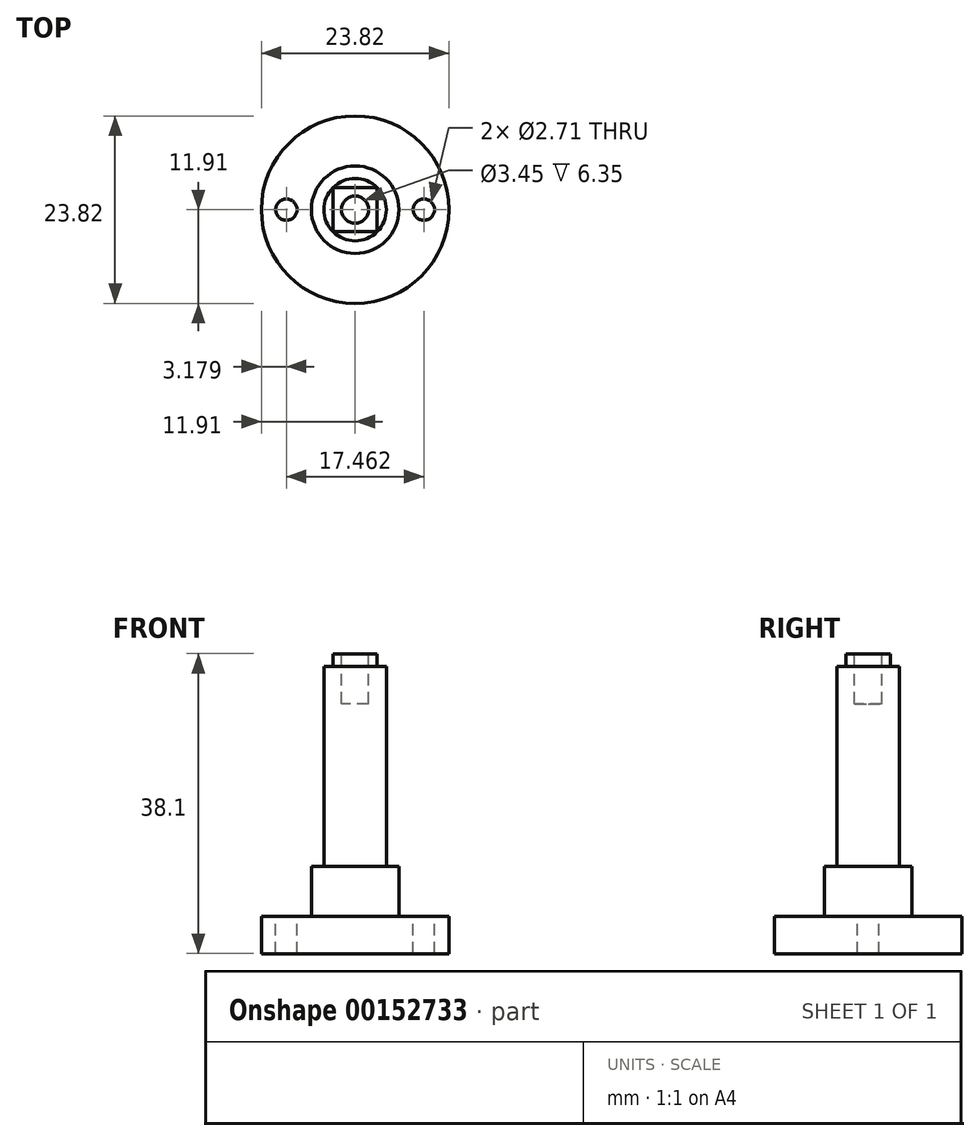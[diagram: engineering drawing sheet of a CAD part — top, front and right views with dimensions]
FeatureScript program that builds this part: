
annotation { "Feature Type Name" : "Feature", "Feature Type Description" : "" }
export const myFeature = defineFeature(function(context is Context, id is Id, definition is map)
    precondition{}
    {
        {
            var Q0;
            Q0=qCreatedBy(makeId("Top.planeOp"),FACE);
            var sketch = newSketch(context, id + "F0", { "sketchPlane" : qUnion([Q0])});
            skCircle(sketch, "E0", {"center": v(0, 0) * mm, "radius": 3.97 * mm});
            skSolve(sketch);
        }
        {
            var Q0;
            Q0 = qSketchRegion(id + "F0", true);
            extrude(context, id + "F1", {"entities" : qUnion([Q0]), "depth" : 25.4 * mm});
        }
        {
            var Q0;
            Q0=makeQuery(id+"F1.opExtrude","CAP_FACE",FACE,{"disambiguationData":[OSD([sQuery(id+"F0.wireOp",EDGE,"E0")])],"isStart":false});
            var sketch = newSketch(context, id + "F2", { "sketchPlane" : qUnion([Q0])});
            skLineSegment(sketch, "E1.bottom", {"start": v(2.8, 2.8) * mm, "end": v(-2.8, 2.8) * mm});
            skLineSegment(sketch, "E1.top", {"start": v(2.8, -2.8) * mm, "end": v(-2.8, -2.8) * mm});
            skLineSegment(sketch, "E1.left", {"start": v(2.8, 2.8) * mm, "end": v(2.8, -2.8) * mm});
            skLineSegment(sketch, "E1.right", {"start": v(-2.8, 2.8) * mm, "end": v(-2.8, -2.8) * mm});
            skPoint(sketch, "E1.middle", {"position": v(0, 0) * mm});
            skSolve(sketch);
        }
        {
            var Q0;
            Q0 = qSketchRegion(id + "F2", true);
            extrude(context, id + "F3", {"entities" : qUnion([Q0]), "operationType" : NewBodyOperationType.ADD, "depth" : 1.59 * mm});
        }
        {
            var Q0;
            Q0=makeQuery(id+"F3.opExtrude","CAP_FACE",FACE,{"disambiguationData":[OSD([sQuery(id+"F2.wireOp",EDGE,"E1.bottom"),sQuery(id+"F2.wireOp",EDGE,"E1.top"),sQuery(id+"F2.wireOp",EDGE,"E1.left"),sQuery(id+"F2.wireOp",EDGE,"E1.right")])],"isStart":false});
            var sketch = newSketch(context, id + "F4", { "sketchPlane" : qUnion([Q0])});
            skCircle(sketch, "E2", {"center": v(0, 0) * mm, "radius": 1.73 * mm});
            skSolve(sketch);
        }
        {
            var Q0;
            Q0 = qSketchRegion(id + "F4", true);
            extrude(context, id + "F5", {"entities" : qUnion([Q0]), "operationType" : NewBodyOperationType.REMOVE, "oppositeDirection" : true, "depth" : 6.35 * mm});
        }
        {
            var Q0;
            Q0=makeQuery(id+"F1.opExtrude","CAP_FACE",FACE,{"disambiguationData":[OSD([sQuery(id+"F0.wireOp",EDGE,"E0")])],"isStart":true});
            var sketch = newSketch(context, id + "F6", { "sketchPlane" : qUnion([Q0])});
            skCircle(sketch, "E3", {"center": v(0, 0) * mm, "radius": 5.56 * mm});
            skSolve(sketch);
        }
        {
            var Q0;
            Q0 = qSketchRegion(id + "F6", true);
            extrude(context, id + "F7", {"entities" : qUnion([Q0]), "operationType" : NewBodyOperationType.ADD, "depth" : 6.35 * mm});
        }
        {
            var Q0;
            Q0=makeQuery(id+"F7.opExtrude","CAP_FACE",FACE,{"disambiguationData":[OSD([sQuery(id+"F6.wireOp",EDGE,"E3")])],"isStart":false});
            var sketch = newSketch(context, id + "F8", { "sketchPlane" : qUnion([Q0])});
            skCircle(sketch, "E4", {"center": v(-8.73, 0) * mm, "radius": 3.18 * mm, "construction": true});
            skCircle(sketch, "E5", {"center": v(0, 0) * mm, "radius": 11.9 * mm});
            skLineSegment(sketch, "E6", {"start": v(8.73, 0) * mm, "end": v(-8.73, 0) * mm, "construction": true});
            skCircle(sketch, "E7", {"center": v(8.73, 0) * mm, "radius": 1.35 * mm});
            skCircle(sketch, "E8", {"center": v(-8.73, 0) * mm, "radius": 1.35 * mm});
            skSolve(sketch);
        }
        {
            var Q0;
            Q0 = qSketchRegion(id + "F8", true);
            extrude(context, id + "F9", {"entities" : qUnion([Q0]), "operationType" : NewBodyOperationType.ADD, "depth" : 4.76 * mm});
        }
    });
